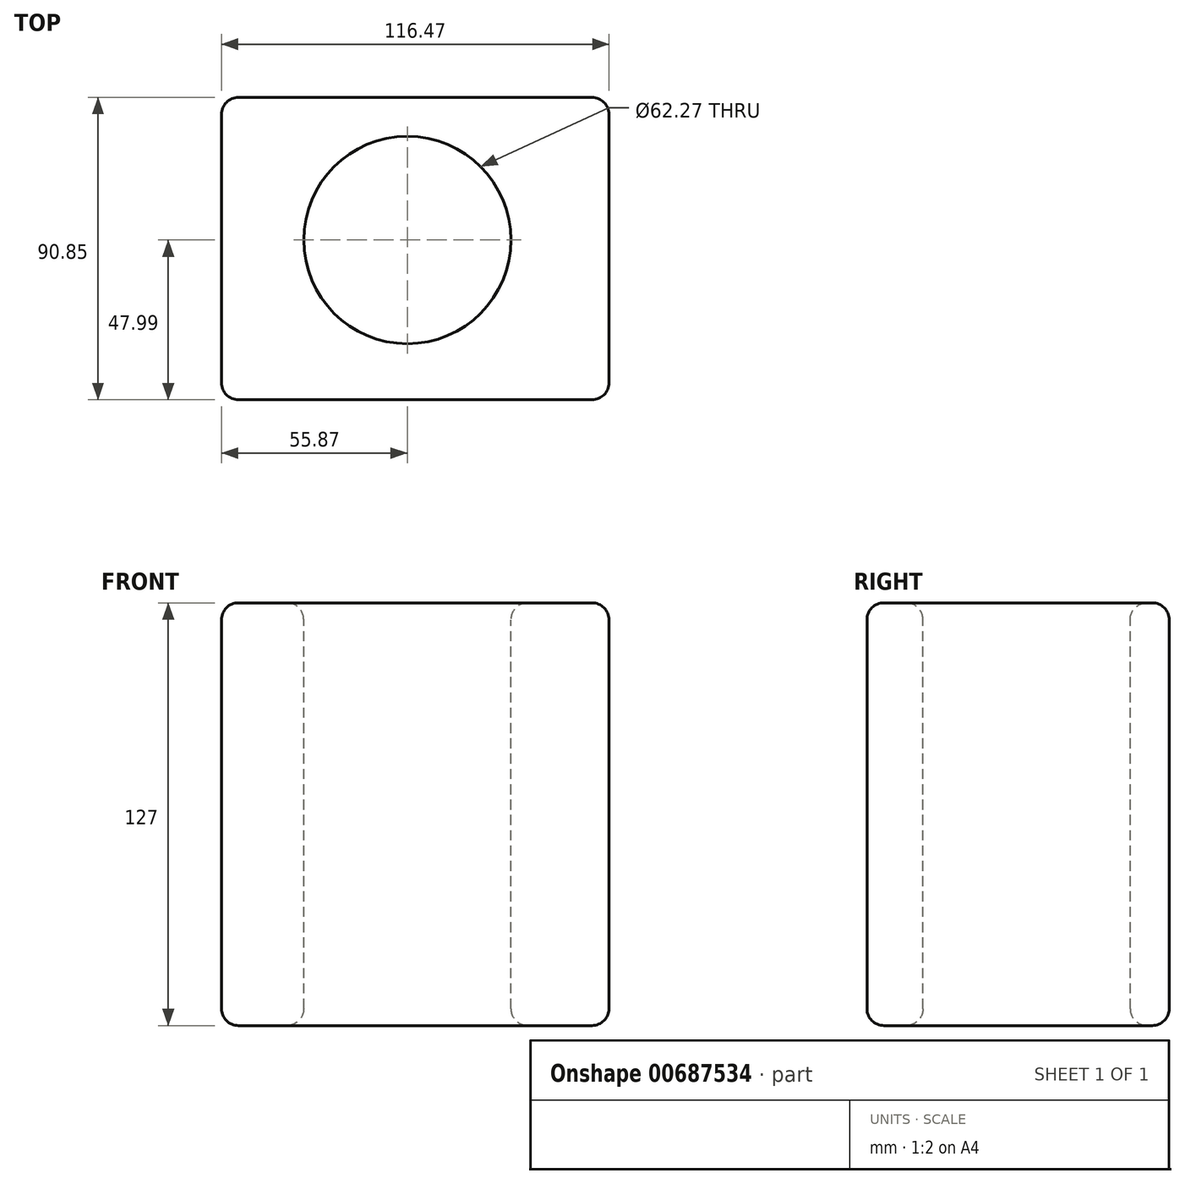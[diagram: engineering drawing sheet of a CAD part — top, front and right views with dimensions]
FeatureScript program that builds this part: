
annotation { "Feature Type Name" : "Feature", "Feature Type Description" : "" }
export const myFeature = defineFeature(function(context is Context, id is Id, definition is map)
    precondition{}
    {
        {
            var Q0;
            Q0=qCreatedBy(makeId("Top.planeOp"),FACE);
            var sketch = newSketch(context, id + "F0", { "sketchPlane" : qUnion([Q0])});
            skLineSegment(sketch, "E0.bottom", {"start": v(-55.87, 42.86) * mm, "end": v(60.6, 42.86) * mm});
            skLineSegment(sketch, "E0.top", {"start": v(-55.87, -47.99) * mm, "end": v(60.6, -47.99) * mm});
            skLineSegment(sketch, "E0.left", {"start": v(-55.87, 42.86) * mm, "end": v(-55.87, -47.99) * mm});
            skLineSegment(sketch, "E0.right", {"start": v(60.6, 42.86) * mm, "end": v(60.6, -47.99) * mm});
            skSolve(sketch);
        }
        {
            var Q0;
            Q0 = qSketchRegion(id + "F0", true);
            extrude(context, id + "F1", {"entities" : qUnion([Q0]), "depth" : 127 * mm, "offsetDistance" : 25.4 * mm});
        }
        {
            var Q0;
            Q0=makeQuery(id+"F1.opExtrude","CAP_FACE",FACE,{"disambiguationData":[OSD([sQuery(id+"F0.wireOp",EDGE,"E0.bottom"),sQuery(id+"F0.wireOp",EDGE,"E0.top"),sQuery(id+"F0.wireOp",EDGE,"E0.left"),sQuery(id+"F0.wireOp",EDGE,"E0.right")])],"isStart":false});
            var sketch = newSketch(context, id + "F2", { "sketchPlane" : qUnion([Q0])});
            skCircle(sketch, "E1", {"center": v(0, 0) * mm, "radius": 31.14 * mm});
            skSolve(sketch);
        }
        {
            var Q0;
            Q0 = qSketchRegion(id + "F2", true);
            extrude(context, id + "F3", {"entities" : qUnion([Q0]), "operationType" : NewBodyOperationType.REMOVE, "oppositeDirection" : true, "depth" : 127 * mm, "offsetDistance" : 25.4 * mm});
        }
        {
            var Q0;
            Q0=makeQuery(id+"F1.opExtrude","CAP_EDGE",EDGE,{"disambiguationData":[OSD([sQuery(id+"F0.wireOp",EDGE,"E0.bottom")])],"isStart":false});
            var Q1;
            Q1=makeQuery(id+"F1.opExtrude","CAP_EDGE",EDGE,{"disambiguationData":[OSD([sQuery(id+"F0.wireOp",EDGE,"E0.left")])],"isStart":false});
            var Q2;
            Q2=makeQuery(id+"F1.opExtrude","CAP_EDGE",EDGE,{"disambiguationData":[OSD([sQuery(id+"F0.wireOp",EDGE,"E0.top")])],"isStart":false});
            var Q3;
            Q3=makeQuery(id+"F1.opExtrude","CAP_EDGE",EDGE,{"disambiguationData":[OSD([sQuery(id+"F0.wireOp",EDGE,"E0.right")])],"isStart":false});
            var Q4;
            Q4=makeQuery(id+"F3.boolean.opBoolean","COPY",EDGE,{"derivedFrom":makeQuery(id+"F3.opExtrude","CAP_EDGE",EDGE,{"disambiguationData":[OSD([sQuery(id+"F2.wireOp",EDGE,"E1")])],"isStart":true})});
            var Q5;
            Q5=makeQuery(id+"F1.opExtrude","SWEPT_EDGE",EDGE,{"disambiguationData":[OSD([sQuery(id+"F0.wireOp",EDGE,"E0.bottom"),sQuery(id+"F0.wireOp",EDGE,"E0.left")])]});
            var Q6;
            Q6=makeQuery(id+"F1.opExtrude","CAP_EDGE",EDGE,{"disambiguationData":[OSD([sQuery(id+"F0.wireOp",EDGE,"E0.left")])],"isStart":true});
            var Q7;
            Q7=makeQuery(id+"F1.opExtrude","SWEPT_EDGE",EDGE,{"disambiguationData":[OSD([sQuery(id+"F0.wireOp",EDGE,"E0.top"),sQuery(id+"F0.wireOp",EDGE,"E0.left")])]});
            var Q8;
            Q8=makeQuery(id+"F1.opExtrude","CAP_EDGE",EDGE,{"disambiguationData":[OSD([sQuery(id+"F0.wireOp",EDGE,"E0.bottom")])],"isStart":true});
            var Q9;
            Q9=makeQuery(id+"F1.opExtrude","SWEPT_EDGE",EDGE,{"disambiguationData":[OSD([sQuery(id+"F0.wireOp",EDGE,"E0.bottom"),sQuery(id+"F0.wireOp",EDGE,"E0.right")])]});
            var Q10;
            Q10=makeQuery(id+"F3.boolean.opBoolean","COPY",FACE,{"derivedFrom":makeQuery(id+"F3.opExtrude","SWEPT_FACE",FACE,{"disambiguationData":[OSD([sQuery(id+"F2.wireOp",EDGE,"E1")])]})});
            var Q11;
            Q11=makeQuery(id+"F3.boolean.opBoolean","COPY",EDGE,{"derivedFrom":makeQuery(id+"F3.opExtrude","CAP_EDGE",EDGE,{"disambiguationData":[OSD([sQuery(id+"F2.wireOp",EDGE,"E1")])],"isStart":false})});
            var Q12;
            Q12=makeQuery(id+"F1.opExtrude","CAP_EDGE",EDGE,{"disambiguationData":[OSD([sQuery(id+"F0.wireOp",EDGE,"E0.right")])],"isStart":true});
            var Q13;
            Q13=makeQuery(id+"F1.opExtrude","CAP_EDGE",EDGE,{"disambiguationData":[OSD([sQuery(id+"F0.wireOp",EDGE,"E0.top")])],"isStart":true});
            var Q14;
            Q14=makeQuery(id+"F1.opExtrude","SWEPT_EDGE",EDGE,{"disambiguationData":[OSD([sQuery(id+"F0.wireOp",EDGE,"E0.top"),sQuery(id+"F0.wireOp",EDGE,"E0.right")])]});
            fillet(context, id + "F4", {"entities" : qUnion([Q0, Q1, Q2, Q3, Q4, Q5, Q6, Q7, Q8, Q9, Q10, Q11, Q12, Q13, Q14]), "radius" : 5.08 * mm, "tangentPropagation" : true, "allowEdgeOverflow" : false});
        }
    });
